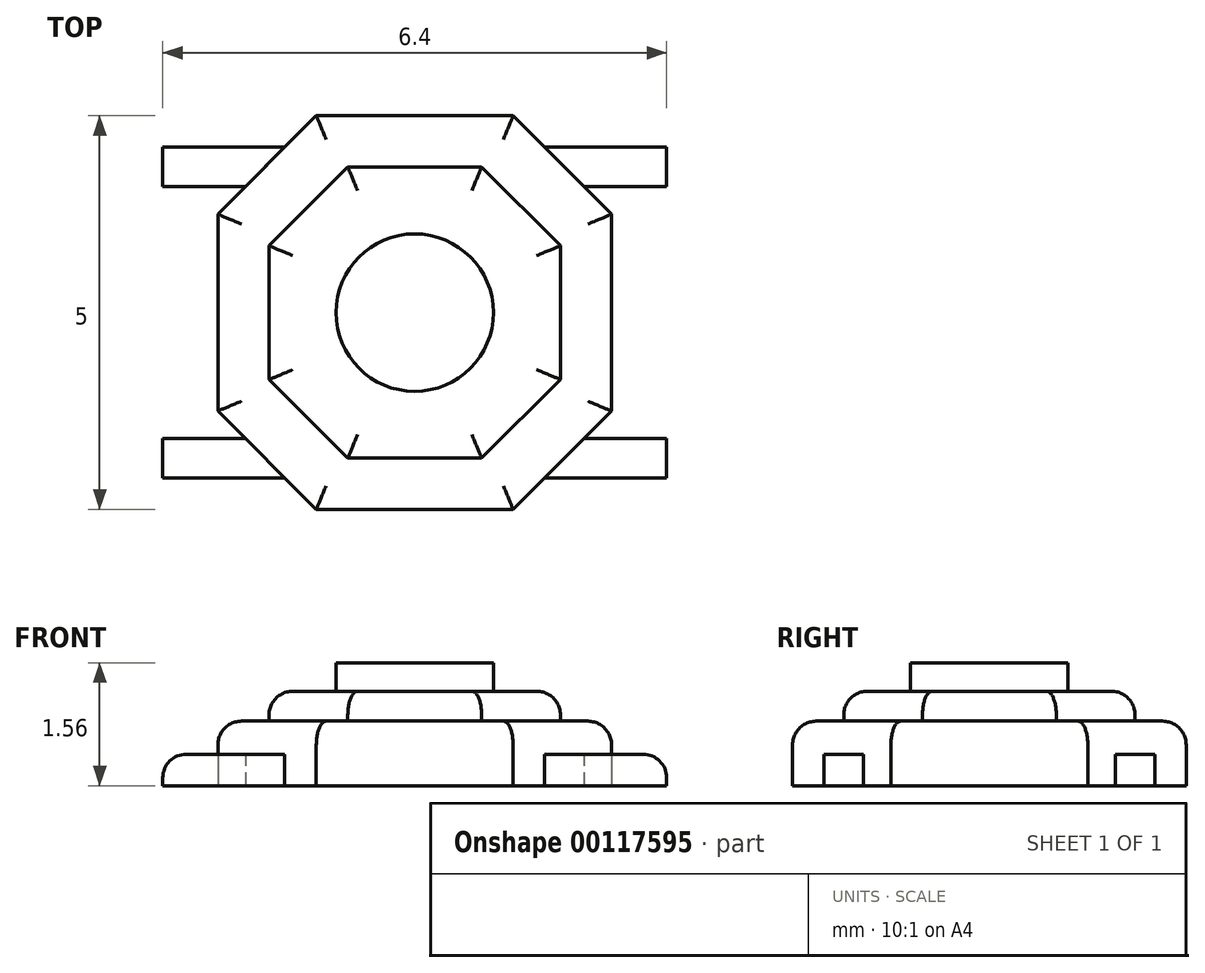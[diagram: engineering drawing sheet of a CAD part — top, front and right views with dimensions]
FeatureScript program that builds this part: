
annotation { "Feature Type Name" : "Feature", "Feature Type Description" : "" }
export const myFeature = defineFeature(function(context is Context, id is Id, definition is map)
    precondition{}
    {
        {
            var Q0;
            Q0=qCreatedBy(makeId("Top.planeOp"),FACE);
            var sketch = newSketch(context, id + "F0", { "sketchPlane" : qUnion([Q0])});
            skLineSegment(sketch, "E0.bottom", {"start": v(-1.25, 2.5) * mm, "end": v(1.25, 2.5) * mm});
            skLineSegment(sketch, "E0.top", {"start": v(-1.25, -2.5) * mm, "end": v(1.25, -2.5) * mm});
            skLineSegment(sketch, "E0.left", {"start": v(-2.5, 1.25) * mm, "end": v(-2.5, -1.25) * mm});
            skLineSegment(sketch, "E0.right", {"start": v(2.5, 1.25) * mm, "end": v(2.5, -1.25) * mm});
            skLineSegment(sketch, "E1", {"start": v(0, 2.5) * mm, "end": v(0, -2.5) * mm, "construction": true});
            skLineSegment(sketch, "E2", {"start": v(-2.5, 0) * mm, "end": v(2.5, 0) * mm, "construction": true});
            skLineSegment(sketch, "E3.bottom", {"start": v(-0.85, 1.85) * mm, "end": v(0.85, 1.85) * mm});
            skLineSegment(sketch, "E3.top", {"start": v(-0.85, -1.85) * mm, "end": v(0.85, -1.85) * mm});
            skLineSegment(sketch, "E3.left", {"start": v(-1.85, 0.85) * mm, "end": v(-1.85, -0.85) * mm});
            skLineSegment(sketch, "E3.right", {"start": v(1.85, 0.85) * mm, "end": v(1.85, -0.85) * mm});
            skCircle(sketch, "E4", {"center": v(0, 0) * mm, "radius": 1 * mm});
            skLineSegment(sketch, "E5", {"start": v(1.65, 2.1) * mm, "end": v(3.2, 2.1) * mm});
            skLineSegment(sketch, "E6", {"start": v(3.2, 2.1) * mm, "end": v(3.2, 1.6) * mm});
            skLineSegment(sketch, "E7", {"start": v(3.2, 1.6) * mm, "end": v(2.15, 1.6) * mm});
            skLineSegment(sketch, "E8", {"start": v(-1.25, 2.5) * mm, "end": v(-2.5, 1.25) * mm});
            skLineSegment(sketch, "E9.MirrorCS", {"start": v(1.25, 2.5) * mm, "end": v(2.5, 1.25) * mm});
            skLineSegment(sketch, "E10.MirrorCS", {"start": v(1.25, -2.5) * mm, "end": v(2.5, -1.25) * mm});
            skLineSegment(sketch, "E11.MirrorCS", {"start": v(-1.25, -2.5) * mm, "end": v(-2.5, -1.25) * mm});
            skPoint(sketch, "E12.orphan", {"position": v(-2.5, 2.5) * mm});
            skPoint(sketch, "E13.orphan", {"position": v(2.5, 2.5) * mm});
            skLineSegment(sketch, "E14.MirrorCS", {"start": v(-3.2, 1.6) * mm, "end": v(-2.15, 1.6) * mm});
            skLineSegment(sketch, "E15.MirrorCS", {"start": v(-3.2, 2.1) * mm, "end": v(-3.2, 1.6) * mm});
            skLineSegment(sketch, "E16.MirrorCS", {"start": v(-1.65, 2.1) * mm, "end": v(-3.2, 2.1) * mm});
            skLineSegment(sketch, "E17.MirrorCS", {"start": v(3.2, -2.1) * mm, "end": v(3.2, -1.6) * mm});
            skLineSegment(sketch, "E18.MirrorCS", {"start": v(3.2, -1.6) * mm, "end": v(2.15, -1.6) * mm});
            skLineSegment(sketch, "E19.MirrorCS", {"start": v(1.65, -2.1) * mm, "end": v(3.2, -2.1) * mm});
            skLineSegment(sketch, "E20.MirrorCS", {"start": v(-3.2, -1.6) * mm, "end": v(-2.15, -1.6) * mm});
            skLineSegment(sketch, "E21.MirrorCS", {"start": v(-3.2, -2.1) * mm, "end": v(-3.2, -1.6) * mm});
            skLineSegment(sketch, "E22.MirrorCS", {"start": v(-1.65, -2.1) * mm, "end": v(-3.2, -2.1) * mm});
            skPoint(sketch, "E23.orphan", {"position": v(-2.5, -2.5) * mm});
            skPoint(sketch, "E24.orphan", {"position": v(2.5, -2.5) * mm});
            skLineSegment(sketch, "E25", {"start": v(-0.85, 1.85) * mm, "end": v(-1.85, 0.85) * mm});
            skLineSegment(sketch, "E26.MirrorCS", {"start": v(0.85, 1.85) * mm, "end": v(1.85, 0.85) * mm});
            skLineSegment(sketch, "E27.MirrorCS", {"start": v(-0.85, -1.85) * mm, "end": v(-1.85, -0.85) * mm});
            skLineSegment(sketch, "E28.MirrorCS", {"start": v(0.85, -1.85) * mm, "end": v(1.85, -0.85) * mm});
            skSolve(sketch);
        }
        {
            var Q0;
            Q0=makeQuery(id+"F0.imprint","IMPRINT",FACE,{"disambiguationData":[TD([[makeQuery(id+"F0.imprint","IMPRINT",EDGE,{"derivedFrom":sQuery(id+"F0.wireOp",EDGE,"E4")}),1.0]])]});
            extrude(context, id + "F1", {"entities" : qUnion([Q0]), "depth" : 1.56 * mm});
        }
        {
            var Q0;
            Q0=makeQuery(id+"F0.imprint","IMPRINT",FACE,{"disambiguationData":[TD([[makeQuery(id+"F0.imprint","IMPRINT",EDGE,{"derivedFrom":sQuery(id+"F0.wireOp",EDGE,"E3.bottom")}),-1.0]])]});
            extrude(context, id + "F2", {"entities" : qUnion([Q0]), "operationType" : NewBodyOperationType.ADD, "depth" : 1.2 * mm});
        }
        {
            var Q0;
            {var subQ14=sQuery(id+"F0.wireOp",EDGE,"E0.bottom");Q0=makeQuery(id+"F0.imprint","IMPRINT",FACE,{"disambiguationData":[TD([[makeQuery(id+"F0.imprint","IMPRINT",EDGE,{"derivedFrom":subQ14}),-1.0]])]});}
            extrude(context, id + "F3", {"entities" : qUnion([Q0]), "operationType" : NewBodyOperationType.ADD, "depth" : 0.82 * mm});
        }
        {
            var Q0;
            {var subQ0=sQuery(id+"F0.wireOp",EDGE,"E14.MirrorCS");Q0=makeQuery(id+"F0.imprint","IMPRINT",FACE,{"disambiguationData":[TD([[makeQuery(id+"F0.imprint","IMPRINT",EDGE,{"derivedFrom":subQ0}),1.0]])]});}
            var Q1;
            {var subQ0=sQuery(id+"F0.wireOp",EDGE,"E20.MirrorCS");Q1=makeQuery(id+"F0.imprint","IMPRINT",FACE,{"disambiguationData":[TD([[makeQuery(id+"F0.imprint","IMPRINT",EDGE,{"derivedFrom":subQ0}),-1.0]])]});}
            var Q2;
            Q2=makeQuery(id+"F0.imprint","IMPRINT",FACE,{"disambiguationData":[TD([[makeQuery(id+"F0.imprint","IMPRINT",EDGE,{"derivedFrom":sQuery(id+"F0.wireOp",EDGE,"E17.MirrorCS")}),1.0]])]});
            var Q3;
            {var subQ0=sQuery(id+"F0.wireOp",EDGE,"E5");Q3=makeQuery(id+"F0.imprint","IMPRINT",FACE,{"disambiguationData":[TD([[makeQuery(id+"F0.imprint","IMPRINT",EDGE,{"derivedFrom":subQ0}),-1.0]])]});}
            extrude(context, id + "F4", {"entities" : qUnion([Q0, Q1, Q2, Q3]), "operationType" : NewBodyOperationType.ADD, "depth" : 0.4 * mm});
        }
        {
            var Q0;
            Q0=makeQuery(id+"F2.opExtrude","CAP_EDGE",EDGE,{"disambiguationData":[OSD([sQuery(id+"F0.wireOp",EDGE,"E25")])],"isStart":false});
            var Q1;
            Q1=makeQuery(id+"F2.opExtrude","CAP_EDGE",EDGE,{"disambiguationData":[OSD([sQuery(id+"F0.wireOp",EDGE,"E3.left")])],"isStart":false});
            var Q2;
            Q2=makeQuery(id+"F2.opExtrude","CAP_EDGE",EDGE,{"disambiguationData":[OSD([sQuery(id+"F0.wireOp",EDGE,"E27.MirrorCS")])],"isStart":false});
            var Q3;
            Q3=makeQuery(id+"F2.opExtrude","CAP_EDGE",EDGE,{"disambiguationData":[OSD([sQuery(id+"F0.wireOp",EDGE,"E3.top")])],"isStart":false});
            var Q4;
            Q4=makeQuery(id+"F2.opExtrude","CAP_EDGE",EDGE,{"disambiguationData":[OSD([sQuery(id+"F0.wireOp",EDGE,"E28.MirrorCS")])],"isStart":false});
            var Q5;
            Q5=makeQuery(id+"F2.opExtrude","CAP_EDGE",EDGE,{"disambiguationData":[OSD([sQuery(id+"F0.wireOp",EDGE,"E3.right")])],"isStart":false});
            var Q6;
            Q6=makeQuery(id+"F2.opExtrude","CAP_EDGE",EDGE,{"disambiguationData":[OSD([sQuery(id+"F0.wireOp",EDGE,"E26.MirrorCS")])],"isStart":false});
            var Q7;
            Q7=makeQuery(id+"F2.opExtrude","CAP_EDGE",EDGE,{"disambiguationData":[OSD([sQuery(id+"F0.wireOp",EDGE,"E3.bottom")])],"isStart":false});
            var Q8;
            Q8=makeQuery(id+"F3.opExtrude","CAP_EDGE",EDGE,{"disambiguationData":[OSD([sQuery(id+"F0.wireOp",EDGE,"E8")])],"isStart":false});
            var Q9;
            Q9=makeQuery(id+"F3.opExtrude","CAP_EDGE",EDGE,{"disambiguationData":[OSD([sQuery(id+"F0.wireOp",EDGE,"E0.left")])],"isStart":false});
            var Q10;
            Q10=makeQuery(id+"F3.opExtrude","CAP_EDGE",EDGE,{"disambiguationData":[OSD([sQuery(id+"F0.wireOp",EDGE,"E11.MirrorCS")])],"isStart":false});
            var Q11;
            Q11=makeQuery(id+"F3.opExtrude","CAP_EDGE",EDGE,{"disambiguationData":[OSD([sQuery(id+"F0.wireOp",EDGE,"E0.top")])],"isStart":false});
            var Q12;
            Q12=makeQuery(id+"F3.opExtrude","CAP_EDGE",EDGE,{"disambiguationData":[OSD([sQuery(id+"F0.wireOp",EDGE,"E10.MirrorCS")])],"isStart":false});
            var Q13;
            Q13=makeQuery(id+"F3.opExtrude","CAP_EDGE",EDGE,{"disambiguationData":[OSD([sQuery(id+"F0.wireOp",EDGE,"E0.right")])],"isStart":false});
            var Q14;
            Q14=makeQuery(id+"F3.opExtrude","CAP_EDGE",EDGE,{"disambiguationData":[OSD([sQuery(id+"F0.wireOp",EDGE,"E9.MirrorCS")])],"isStart":false});
            var Q15;
            Q15=makeQuery(id+"F3.opExtrude","CAP_EDGE",EDGE,{"disambiguationData":[OSD([sQuery(id+"F0.wireOp",EDGE,"E0.bottom")])],"isStart":false});
            var Q16;
            Q16=makeQuery(id+"F4.opExtrude","CAP_EDGE",EDGE,{"disambiguationData":[OSD([sQuery(id+"F0.wireOp",EDGE,"E15.MirrorCS")])],"isStart":false});
            var Q17;
            Q17=makeQuery(id+"F4.opExtrude","CAP_EDGE",EDGE,{"disambiguationData":[OSD([sQuery(id+"F0.wireOp",EDGE,"E21.MirrorCS")])],"isStart":false});
            var Q18;
            Q18=makeQuery(id+"F4.opExtrude","CAP_EDGE",EDGE,{"disambiguationData":[OSD([sQuery(id+"F0.wireOp",EDGE,"E17.MirrorCS")])],"isStart":false});
            var Q19;
            Q19=makeQuery(id+"F4.opExtrude","CAP_EDGE",EDGE,{"disambiguationData":[OSD([sQuery(id+"F0.wireOp",EDGE,"E6")])],"isStart":false});
            fillet(context, id + "F5", {"entities" : qUnion([Q0, Q1, Q2, Q3, Q4, Q5, Q6, Q7, Q8, Q9, Q10, Q11, Q12, Q13, Q14, Q15, Q16, Q17, Q18, Q19]), "radius" : 0.3 * mm, "tangentPropagation" : true, "allowEdgeOverflow" : false});
        }
    });
